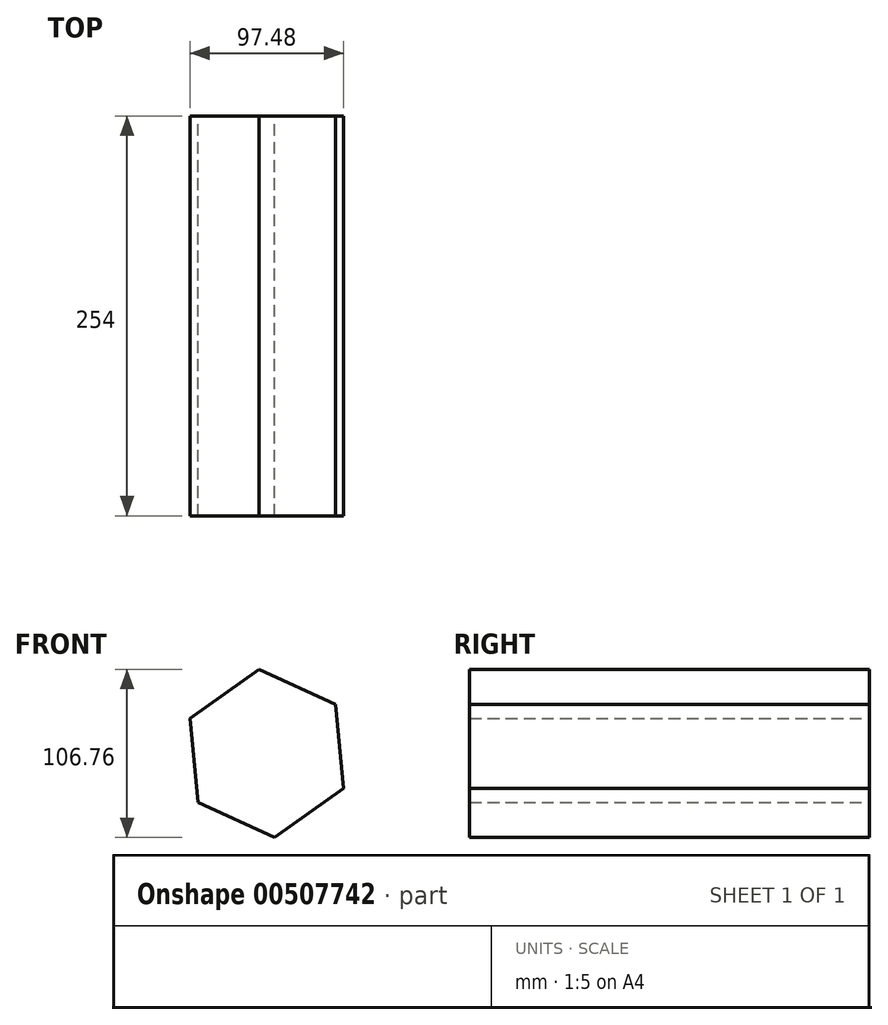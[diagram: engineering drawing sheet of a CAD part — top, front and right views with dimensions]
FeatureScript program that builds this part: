
annotation { "Feature Type Name" : "Feature", "Feature Type Description" : "" }
export const myFeature = defineFeature(function(context is Context, id is Id, definition is map)
    precondition{}
    {
        {
            var Q0;
            Q0=qCreatedBy(makeId("Front.planeOp"),FACE);
            var sketch = newSketch(context, id + "F0", { "sketchPlane" : qUnion([Q0])});
            skCircle(sketch, "E0.cCircle", {"center": v(0, 0) * mm, "radius": 53.62 * mm, "construction": true});
            skLineSegment(sketch, "E0.0", {"start": v(43.72, 31.04) * mm, "end": v(48.74, -22.34) * mm});
            skLineSegment(sketch, "E0.1", {"start": v(48.74, -22.34) * mm, "end": v(5.02, -53.38) * mm});
            skLineSegment(sketch, "E0.2", {"start": v(5.02, -53.38) * mm, "end": v(-43.72, -31.04) * mm});
            skLineSegment(sketch, "E0.3", {"start": v(-43.72, -31.04) * mm, "end": v(-48.74, 22.34) * mm});
            skLineSegment(sketch, "E0.4", {"start": v(-48.74, 22.34) * mm, "end": v(-5.02, 53.38) * mm});
            skLineSegment(sketch, "E0.5", {"start": v(-5.02, 53.38) * mm, "end": v(43.72, 31.04) * mm});
            skSolve(sketch);
        }
        {
            var Q0;
            Q0=makeQuery(id+"F0.imprint","IMPRINT",FACE,{"disambiguationData":[TD([[makeQuery(id+"F0.imprint","IMPRINT",EDGE,{"derivedFrom":sQuery(id+"F0.wireOp",EDGE,"E0.0")}),-1.0]])]});
            extrude(context, id + "F1", {"entities" : qUnion([Q0]), "depth" : 254 * mm});
        }
    });
